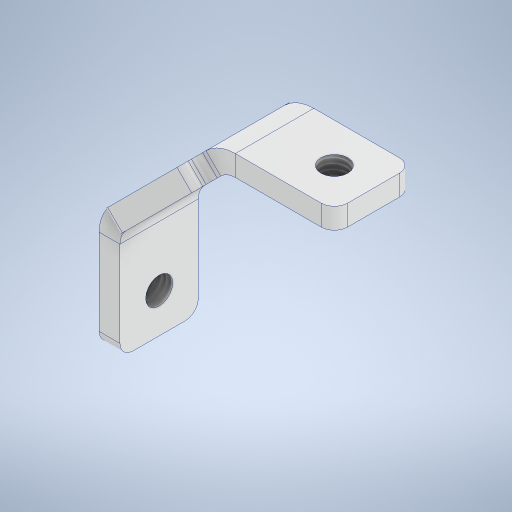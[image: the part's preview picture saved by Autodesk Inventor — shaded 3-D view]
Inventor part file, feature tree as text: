
AUTODESK INVENTOR PART (.ipt)
format: ipt  version: 2024 (Build 280153000, 153)  size: 350,208 bytes
history: native  units: mm
features: sheet_metal_op x5, sketch x4, hole x3, fillet x2, other x2
ambient origin geometry x8: Origin, YZ Plane, XZ Plane, XY Plane, X Axis, Y Axis, Z Axis, Center Point
bodies: Solid1 (feature_tree)
feature tree (16):
  sheet_metal_op  "Contour Flange1"
  hole  "Hole1"  [1 undecoded]
  hole  "Hole2"  [1 undecoded]
  sketch  "Sketch4"  dims[d8=1.5875mm d9=6.35mm d10=3.175mm d11=12.0mm d12=3.175mm d13=3.175mm d14=12.7mm d15=3.175mm d16=3.175mm d17=4.134mm d18=10.0mm d19=4.0mm d20=2.0mm d21=90.0deg d22=3.175mm d23=20.594885mm d24=6.0mm d25=4.134mm d26=10.0mm d27=4.0mm d28=2.0mm d29=90.0deg d30=8.0mm d31=20.594885mm d32=17.0mm d34=3.175mm d35=3.175mm d36=1.5875mm d37=6.35mm d38=3.175mm d39=1.0mm d40=2.0mm d41=6.3mm d42=10.0mm d43=4.0mm d44=2.0mm d45=90.0deg d46=8.0mm d47=20.594885mm]
  sheet_metal_op  "Face1"
  fillet  "Fillet1"  Radius=37.5mm
  fillet  "Fillet2"  Radius=37.5mm
  hole  "Hole3"  [1 undecoded]
  sketch  "Sketch1"  dims[d0=30.0mm d1=3.0mm]
  other  "Plate1"
  sheet_metal_op  "Bend1"
  sheet_metal_op  "Corner1"
  sketch  "Sketch2"  dims[d2=31.5mm d3=6.0mm d4=37.5mm d5=37.5mm]
  sketch  "Sketch3"  dims[d6=3.175mm d7=3.175mm]
  other  "Plate2"
  sheet_metal_op  "Bend2"
note: 3 required parameter values undecoded (feature->parameter linkage not recoverable at this tier; creation-order binding heuristic only, values carry confidence <= 0.55)
